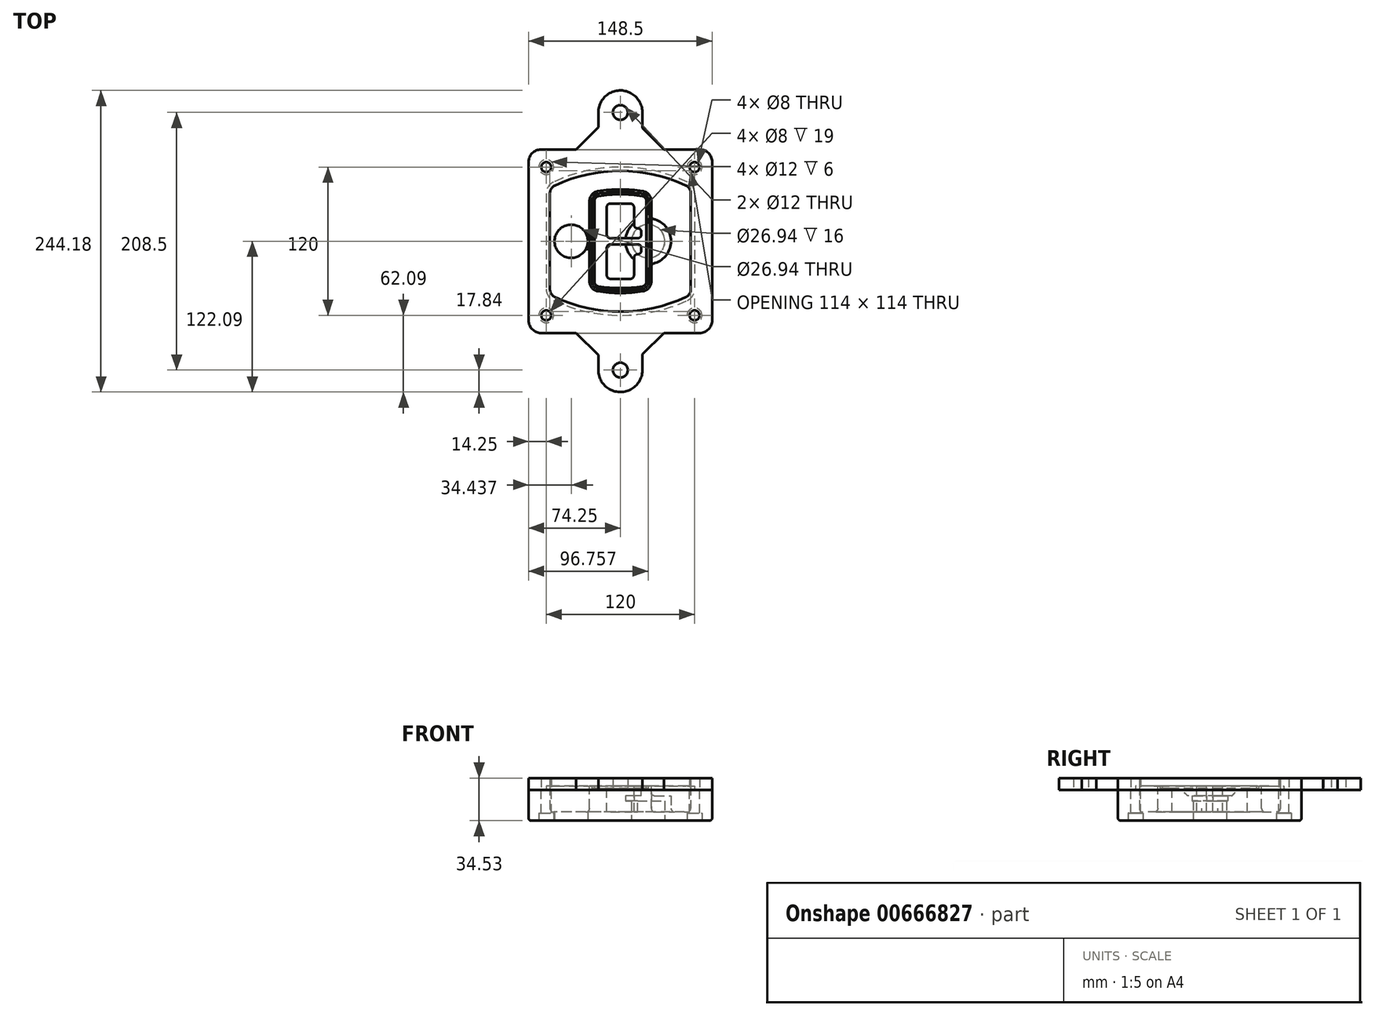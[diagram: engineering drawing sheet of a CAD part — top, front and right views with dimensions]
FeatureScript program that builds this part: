
annotation { "Feature Type Name" : "Feature", "Feature Type Description" : "" }
export const myFeature = defineFeature(function(context is Context, id is Id, definition is map)
    precondition{}
    {
        {
            var Q0;
            Q0=qCreatedBy(makeId("Top.planeOp"),FACE);
            var sketch = newSketch(context, id + "F0", { "sketchPlane" : qUnion([Q0])});
            skPoint(sketch, "E0.rect.middle", {"position": v(0, 0) * mm});
            skLineSegment(sketch, "E1.bottom", {"start": v(-64.25, -74.25) * mm, "end": v(64.25, -74.25) * mm});
            skLineSegment(sketch, "E1.top", {"start": v(-64.25, 74.25) * mm, "end": v(64.25, 74.25) * mm});
            skLineSegment(sketch, "E1.left", {"start": v(-74.25, -64.25) * mm, "end": v(-74.25, 64.25) * mm});
            skLineSegment(sketch, "E1.right", {"start": v(74.25, -64.25) * mm, "end": v(74.25, 64.25) * mm});
            skLineSegment(sketch, "E2", {"start": v(-74.25, 74.25) * mm, "end": v(74.25, -74.25) * mm, "construction": true});
            skLineSegment(sketch, "E3", {"start": v(74.25, 74.25) * mm, "end": v(-74.25, -74.25) * mm, "construction": true});
            skCircle(sketch, "E4", {"center": v(-60, 60) * mm, "radius": 4 * mm});
            skCircle(sketch, "E5", {"center": v(60, 60) * mm, "radius": 4 * mm});
            skCircle(sketch, "E6", {"center": v(60, -60) * mm, "radius": 4 * mm});
            skCircle(sketch, "E7", {"center": v(-60, -60) * mm, "radius": 4 * mm});
            skLineSegment(sketch, "E8", {"start": v(-60, 60) * mm, "end": v(60, 60) * mm, "construction": true});
            skLineSegment(sketch, "E9", {"start": v(60, 60) * mm, "end": v(60, -60) * mm, "construction": true});
            skLineSegment(sketch, "E10", {"start": v(60, -60) * mm, "end": v(-60, -60) * mm, "construction": true});
            skLineSegment(sketch, "E11", {"start": v(-60, -60) * mm, "end": v(-60, 60) * mm, "construction": true});
            skLineSegment(sketch, "E12", {"start": v(-60, 38.83) * mm, "end": v(-60, -38.83) * mm});
            skLineSegment(sketch, "E13", {"start": v(60, 38.83) * mm, "end": v(60, -38.83) * mm});
            skArc(sketch, "E14", {"start": v(54.26, 47.88) * mm, "mid": v(0, 60) * mm, "end": v(-54.26, 47.88) * mm});
            skArc(sketch, "E15", {"start": v(-54.26, -47.88) * mm, "mid": v(0, -60) * mm, "end": v(54.26, -47.88) * mm});
            skLineSegment(sketch, "E16", {"start": v(-60, 0) * mm, "end": v(60, 0) * mm, "construction": true});
            skPoint(sketch, "E17.visualSharp", {"position": v(-60, -45) * mm});
            skArc(sketch, "E17.filletArc", {"start": v(-60, -38.83) * mm, "mid": v(-58.44, -44.2) * mm, "end": v(-54.26, -47.88) * mm});
            skPoint(sketch, "E18.visualSharp", {"position": v(-60, 45) * mm});
            skArc(sketch, "E18.filletArc", {"start": v(-54.26, 47.88) * mm, "mid": v(-58.44, 44.2) * mm, "end": v(-60, 38.83) * mm});
            skPoint(sketch, "E19.visualSharp", {"position": v(60, 45) * mm});
            skArc(sketch, "E19.filletArc", {"start": v(60, 38.83) * mm, "mid": v(58.44, 44.2) * mm, "end": v(54.26, 47.88) * mm});
            skPoint(sketch, "E20.visualSharp", {"position": v(60, -45) * mm});
            skArc(sketch, "E20.filletArc", {"start": v(54.26, -47.88) * mm, "mid": v(58.44, -44.2) * mm, "end": v(60, -38.83) * mm});
            skPoint(sketch, "E21.visualSharp", {"position": v(-74.25, 74.25) * mm});
            skArc(sketch, "E21.filletArc", {"start": v(-64.25, 74.25) * mm, "mid": v(-71.32, 71.32) * mm, "end": v(-74.25, 64.25) * mm});
            skPoint(sketch, "E22.visualSharp", {"position": v(74.25, 74.25) * mm});
            skArc(sketch, "E22.filletArc", {"start": v(74.25, 64.25) * mm, "mid": v(71.32, 71.32) * mm, "end": v(64.25, 74.25) * mm});
            skPoint(sketch, "E23.visualSharp", {"position": v(74.25, -74.25) * mm});
            skArc(sketch, "E23.filletArc", {"start": v(64.25, -74.25) * mm, "mid": v(71.32, -71.32) * mm, "end": v(74.25, -64.25) * mm});
            skPoint(sketch, "E24.visualSharp", {"position": v(-74.25, -74.25) * mm});
            skArc(sketch, "E24.filletArc", {"start": v(-74.25, -64.25) * mm, "mid": v(-71.32, -71.32) * mm, "end": v(-64.25, -74.25) * mm});
            skArc(sketch, "E25.0", {"start": v(57, 38.83) * mm, "mid": v(55.9, 42.58) * mm, "end": v(52.98, 45.17) * mm});
            skLineSegment(sketch, "E25.1", {"start": v(57, 38.83) * mm, "end": v(57, -38.83) * mm});
            skArc(sketch, "E25.2", {"start": v(52.98, -45.17) * mm, "mid": v(55.9, -42.58) * mm, "end": v(57, -38.83) * mm});
            skArc(sketch, "E25.3", {"start": v(-52.98, -45.17) * mm, "mid": v(0, -57) * mm, "end": v(52.98, -45.17) * mm});
            skArc(sketch, "E25.4", {"start": v(-57, -38.83) * mm, "mid": v(-55.9, -42.58) * mm, "end": v(-52.98, -45.17) * mm});
            skArc(sketch, "E25.5", {"start": v(52.98, 45.17) * mm, "mid": v(0, 57) * mm, "end": v(-52.98, 45.17) * mm});
            skLineSegment(sketch, "E25.6", {"start": v(-57, 38.83) * mm, "end": v(-57, -38.83) * mm});
            skArc(sketch, "E25.7", {"start": v(-52.98, 45.17) * mm, "mid": v(-55.9, 42.58) * mm, "end": v(-57, 38.83) * mm});
            skArc(sketch, "E26.0", {"start": v(-55.96, 51.5) * mm, "mid": v(-61.82, 46.33) * mm, "end": v(-64, 38.83) * mm});
            skArc(sketch, "E26.1", {"start": v(55.96, 51.5) * mm, "mid": v(0, 64) * mm, "end": v(-55.96, 51.5) * mm});
            skArc(sketch, "E26.2", {"start": v(64, 38.83) * mm, "mid": v(61.82, 46.33) * mm, "end": v(55.96, 51.5) * mm});
            skLineSegment(sketch, "E26.3", {"start": v(64, 38.83) * mm, "end": v(64, -38.83) * mm});
            skArc(sketch, "E26.4", {"start": v(55.96, -51.5) * mm, "mid": v(61.82, -46.33) * mm, "end": v(64, -38.83) * mm});
            skLineSegment(sketch, "E26.5", {"start": v(-64, 38.83) * mm, "end": v(-64, -38.83) * mm});
            skArc(sketch, "E26.6", {"start": v(-55.96, -51.5) * mm, "mid": v(0, -64) * mm, "end": v(55.96, -51.5) * mm});
            skArc(sketch, "E26.7", {"start": v(-64, -38.83) * mm, "mid": v(-61.82, -46.33) * mm, "end": v(-55.96, -51.5) * mm});
            skSolve(sketch);
        }
        {
            var Q0;
            Q0=makeQuery(id+"F0.imprint","IMPRINT",FACE,{"disambiguationData":[TD([[makeQuery(id+"F0.imprint","IMPRINT",EDGE,{"derivedFrom":sQuery(id+"F0.wireOp",EDGE,"E1.bottom")}),1.0]])]});
            var Q1;
            Q1=makeQuery(id+"F0.imprint","IMPRINT",FACE,{"disambiguationData":[TD([[makeQuery(id+"F0.imprint","IMPRINT",EDGE,{"derivedFrom":sQuery(id+"F0.wireOp",EDGE,"E12")}),1.0]])]});
            var Q2;
            Q2=makeQuery(id+"F0.imprint","IMPRINT",FACE,{"disambiguationData":[TD([[makeQuery(id+"F0.imprint","IMPRINT",EDGE,{"derivedFrom":sQuery(id+"F0.wireOp",EDGE,"E25.0")}),1.0]])]});
            var Q3;
            Q3=makeQuery(id+"F0.imprint","IMPRINT",FACE,{"disambiguationData":[TD([[makeQuery(id+"F0.imprint","IMPRINT",EDGE,{"derivedFrom":sQuery(id+"F0.wireOp",EDGE,"E12")}),-1.0]])]});
            extrude(context, id + "F1", {"entities" : qUnion([Q0, Q1, Q2, Q3]), "oppositeDirection" : true, "depth" : 25 * mm});
        }
        {
            var Q0;
            Q0=makeQuery(id+"F0.imprint","IMPRINT",FACE,{"disambiguationData":[TD([[makeQuery(id+"F0.imprint","IMPRINT",EDGE,{"derivedFrom":sQuery(id+"F0.wireOp",EDGE,"E12")}),1.0]])]});
            extrude(context, id + "F2", {"entities" : qUnion([Q0]), "operationType" : NewBodyOperationType.ADD, "depth" : 3 * mm});
        }
        {
            var Q0;
            Q0=makeQuery(id+"F0.imprint","IMPRINT",FACE,{"disambiguationData":[TD([[makeQuery(id+"F0.imprint","IMPRINT",EDGE,{"derivedFrom":sQuery(id+"F0.wireOp",EDGE,"E25.0")}),1.0]])]});
            extrude(context, id + "F3", {"entities" : qUnion([Q0]), "operationType" : NewBodyOperationType.REMOVE, "oppositeDirection" : true, "depth" : 18 * mm});
        }
        {
            var Q0;
            Q0=makeQuery(id+"F2.opExtrude","CAP_FACE",FACE,{"disambiguationData":[OSD([sQuery(id+"F0.wireOp",EDGE,"E12"),sQuery(id+"F0.wireOp",EDGE,"E13"),sQuery(id+"F0.wireOp",EDGE,"E14"),sQuery(id+"F0.wireOp",EDGE,"E15"),sQuery(id+"F0.wireOp",EDGE,"E17.filletArc"),sQuery(id+"F0.wireOp",EDGE,"E18.filletArc"),sQuery(id+"F0.wireOp",EDGE,"E19.filletArc"),sQuery(id+"F0.wireOp",EDGE,"E20.filletArc"),sQuery(id+"F0.wireOp",EDGE,"E25.0"),sQuery(id+"F0.wireOp",EDGE,"E25.1"),sQuery(id+"F0.wireOp",EDGE,"E25.2"),sQuery(id+"F0.wireOp",EDGE,"E25.3"),sQuery(id+"F0.wireOp",EDGE,"E25.4"),sQuery(id+"F0.wireOp",EDGE,"E25.5"),sQuery(id+"F0.wireOp",EDGE,"E25.6"),sQuery(id+"F0.wireOp",EDGE,"E25.7")])],"isStart":false});
            var sketch = newSketch(context, id + "F4", { "sketchPlane" : qUnion([Q0])});
            skArc(sketch, "E27.0", {"start": v(-18.34, -40.45) * mm, "mid": v(0, -42) * mm, "end": v(18.34, -40.45) * mm});
            skArc(sketch, "E28.0", {"start": v(18.34, 40.45) * mm, "mid": v(0, 42) * mm, "end": v(-18.34, 40.45) * mm});
            skLineSegment(sketch, "E29", {"start": v(-25, 32.57) * mm, "end": v(-25, -32.57) * mm});
            skLineSegment(sketch, "E30", {"start": v(25, 32.57) * mm, "end": v(25, -32.57) * mm});
            skLineSegment(sketch, "E31", {"start": v(-25, 39.1) * mm, "end": v(25, 39.1) * mm, "construction": true});
            skLineSegment(sketch, "E32", {"start": v(-25, -39.1) * mm, "end": v(25, -39.1) * mm, "construction": true});
            skPoint(sketch, "E33.visualSharp", {"position": v(-25, 39.1) * mm});
            skArc(sketch, "E33.filletArc", {"start": v(-18.34, 40.45) * mm, "mid": v(-23.11, 37.73) * mm, "end": v(-25, 32.57) * mm});
            skPoint(sketch, "E34.visualSharp", {"position": v(25, 39.1) * mm});
            skArc(sketch, "E34.filletArc", {"start": v(25, 32.57) * mm, "mid": v(23.11, 37.73) * mm, "end": v(18.34, 40.45) * mm});
            skPoint(sketch, "E35.visualSharp", {"position": v(25, -39.1) * mm});
            skArc(sketch, "E35.filletArc", {"start": v(18.34, -40.45) * mm, "mid": v(23.11, -37.73) * mm, "end": v(25, -32.57) * mm});
            skPoint(sketch, "E36.visualSharp", {"position": v(-25, -39.1) * mm});
            skArc(sketch, "E36.filletArc", {"start": v(-25, -32.57) * mm, "mid": v(-23.11, -37.73) * mm, "end": v(-18.34, -40.45) * mm});
            skArc(sketch, "E37.0", {"start": v(52.98, 45.17) * mm, "mid": v(0, 57) * mm, "end": v(-52.98, 45.17) * mm});
            skArc(sketch, "E37.1", {"start": v(-52.98, 45.17) * mm, "mid": v(-55.9, 42.58) * mm, "end": v(-57, 38.83) * mm});
            skLineSegment(sketch, "E37.2", {"start": v(-57, 38.83) * mm, "end": v(-57, -38.83) * mm});
            skArc(sketch, "E37.3", {"start": v(-57, -38.83) * mm, "mid": v(-55.9, -42.58) * mm, "end": v(-52.98, -45.17) * mm});
            skArc(sketch, "E37.4", {"start": v(-52.98, -45.17) * mm, "mid": v(0, -57) * mm, "end": v(52.98, -45.17) * mm});
            skArc(sketch, "E37.5", {"start": v(52.98, -45.17) * mm, "mid": v(55.9, -42.58) * mm, "end": v(57, -38.83) * mm});
            skLineSegment(sketch, "E37.6", {"start": v(57, 38.83) * mm, "end": v(57, -38.83) * mm});
            skArc(sketch, "E37.7", {"start": v(57, 38.83) * mm, "mid": v(55.9, 42.58) * mm, "end": v(52.98, 45.17) * mm});
            skLineSegment(sketch, "E38.0", {"start": v(23, 32.57) * mm, "end": v(23, -32.57) * mm});
            skArc(sketch, "E38.1", {"start": v(18, -38.48) * mm, "mid": v(21.58, -36.44) * mm, "end": v(23, -32.57) * mm});
            skArc(sketch, "E38.2", {"start": v(-18, -38.48) * mm, "mid": v(0, -40) * mm, "end": v(18, -38.48) * mm});
            skArc(sketch, "E38.3", {"start": v(-23, -32.57) * mm, "mid": v(-21.58, -36.44) * mm, "end": v(-18, -38.48) * mm});
            skLineSegment(sketch, "E38.4", {"start": v(-23, 32.57) * mm, "end": v(-23, -32.57) * mm});
            skArc(sketch, "E38.5", {"start": v(23, 32.57) * mm, "mid": v(21.58, 36.44) * mm, "end": v(18, 38.48) * mm});
            skArc(sketch, "E38.6", {"start": v(-18, 38.48) * mm, "mid": v(-21.58, 36.44) * mm, "end": v(-23, 32.57) * mm});
            skArc(sketch, "E38.7", {"start": v(18, 38.48) * mm, "mid": v(0, 40) * mm, "end": v(-18, 38.48) * mm});
            skArc(sketch, "E39.0", {"start": v(21, 32.57) * mm, "mid": v(20.06, 35.15) * mm, "end": v(17.67, 36.5) * mm});
            skLineSegment(sketch, "E39.1", {"start": v(21, 32.57) * mm, "end": v(21, -32.57) * mm});
            skArc(sketch, "E39.2", {"start": v(17.67, -36.5) * mm, "mid": v(20.06, -35.15) * mm, "end": v(21, -32.57) * mm});
            skArc(sketch, "E39.3", {"start": v(-17.67, -36.5) * mm, "mid": v(0, -38) * mm, "end": v(17.67, -36.5) * mm});
            skArc(sketch, "E39.4", {"start": v(-21, -32.57) * mm, "mid": v(-20.06, -35.15) * mm, "end": v(-17.67, -36.5) * mm});
            skArc(sketch, "E39.5", {"start": v(17.67, 36.5) * mm, "mid": v(0, 38) * mm, "end": v(-17.67, 36.5) * mm});
            skLineSegment(sketch, "E39.6", {"start": v(-21, 32.57) * mm, "end": v(-21, -32.57) * mm});
            skArc(sketch, "E39.7", {"start": v(-17.67, 36.5) * mm, "mid": v(-20.06, 35.15) * mm, "end": v(-21, 32.57) * mm});
            skLineSegment(sketch, "E40", {"start": v(-25, 0) * mm, "end": v(25, 0) * mm, "construction": true});
            skLineSegment(sketch, "E41", {"start": v(-11, 5.5) * mm, "end": v(-11, 27.5) * mm});
            skLineSegment(sketch, "E42", {"start": v(-8, 30.5) * mm, "end": v(8, 30.5) * mm});
            skLineSegment(sketch, "E43", {"start": v(11, 27.5) * mm, "end": v(11, 13.5) * mm});
            skLineSegment(sketch, "E44", {"start": v(14, 10.5) * mm, "end": v(14, 10.5) * mm});
            skLineSegment(sketch, "E45", {"start": v(17, 7.5) * mm, "end": v(17, 5.5) * mm});
            skLineSegment(sketch, "E46", {"start": v(14, 2.5) * mm, "end": v(-8, 2.5) * mm});
            skPoint(sketch, "E47.visualSharp", {"position": v(-11, 30.5) * mm});
            skArc(sketch, "E47.filletArc", {"start": v(-8, 30.5) * mm, "mid": v(-10.12, 29.62) * mm, "end": v(-11, 27.5) * mm});
            skPoint(sketch, "E48.visualSharp", {"position": v(11, 30.5) * mm});
            skArc(sketch, "E48.filletArc", {"start": v(11, 27.5) * mm, "mid": v(10.12, 29.62) * mm, "end": v(8, 30.5) * mm});
            skPoint(sketch, "E49.visualSharp", {"position": v(11, 10.5) * mm});
            skArc(sketch, "E49.filletArc", {"start": v(11, 13.5) * mm, "mid": v(11.88, 11.38) * mm, "end": v(14, 10.5) * mm});
            skPoint(sketch, "E50.visualSharp", {"position": v(17, 10.5) * mm});
            skArc(sketch, "E50.filletArc", {"start": v(17, 7.5) * mm, "mid": v(16.12, 9.62) * mm, "end": v(14, 10.5) * mm});
            skPoint(sketch, "E51.visualSharp", {"position": v(17, 2.5) * mm});
            skArc(sketch, "E51.filletArc", {"start": v(14, 2.5) * mm, "mid": v(16.12, 3.38) * mm, "end": v(17, 5.5) * mm});
            skPoint(sketch, "E52.visualSharp", {"position": v(-11, 2.5) * mm});
            skArc(sketch, "E52.filletArc", {"start": v(-11, 5.5) * mm, "mid": v(-10.12, 3.38) * mm, "end": v(-8, 2.5) * mm});
            skLineSegment(sketch, "E53.0.MirrorCS", {"start": v(14, -2.5) * mm, "end": v(-8, -2.5) * mm});
            skArc(sketch, "E54.0.MirrorCS", {"start": v(-11, -5.5) * mm, "mid": v(-10.12, -3.38) * mm, "end": v(-8, -2.5) * mm});
            skLineSegment(sketch, "E55.0.MirrorCS", {"start": v(-11, -5.5) * mm, "end": v(-11, -27.5) * mm});
            skArc(sketch, "E56.0.MirrorCS", {"start": v(-8, -30.5) * mm, "mid": v(-10.12, -29.62) * mm, "end": v(-11, -27.5) * mm});
            skLineSegment(sketch, "E57.0.MirrorCS", {"start": v(-8, -30.5) * mm, "end": v(8, -30.5) * mm});
            skArc(sketch, "E58.0.MirrorCS", {"start": v(11, -27.5) * mm, "mid": v(10.12, -29.62) * mm, "end": v(8, -30.5) * mm});
            skLineSegment(sketch, "E59.0.MirrorCS", {"start": v(11, -27.5) * mm, "end": v(11, -13.5) * mm});
            skArc(sketch, "E60.0.MirrorCS", {"start": v(11, -13.5) * mm, "mid": v(11.88, -11.38) * mm, "end": v(14, -10.5) * mm});
            skArc(sketch, "E61.0.MirrorCS", {"start": v(17, -7.5) * mm, "mid": v(16.12, -9.62) * mm, "end": v(14, -10.5) * mm});
            skLineSegment(sketch, "E62.0.MirrorCS", {"start": v(17, -7.5) * mm, "end": v(17, -5.5) * mm});
            skArc(sketch, "E63.0.MirrorCS", {"start": v(14, -2.5) * mm, "mid": v(16.12, -3.38) * mm, "end": v(17, -5.5) * mm});
            skSolve(sketch);
        }
        {
            var Q0;
            Q0=makeQuery(id+"F4.imprint","IMPRINT",FACE,{"disambiguationData":[TD([[makeQuery(id+"F4.imprint","IMPRINT",EDGE,{"derivedFrom":sQuery(id+"F4.wireOp",EDGE,"E27.0")}),1.0]])]});
            var Q1;
            Q1=makeQuery(id+"F4.imprint","IMPRINT",FACE,{"disambiguationData":[TD([[makeQuery(id+"F4.imprint","IMPRINT",EDGE,{"derivedFrom":sQuery(id+"F4.wireOp",EDGE,"E38.0")}),-1.0]])]});
            var Q2;
            Q2=makeQuery(id+"F4.imprint","IMPRINT",FACE,{"disambiguationData":[TD([[makeQuery(id+"F4.imprint","IMPRINT",EDGE,{"derivedFrom":sQuery(id+"F4.wireOp",EDGE,"E39.0")}),1.0]])]});
            extrude(context, id + "F5", {"entities" : qUnion([Q0, Q1, Q2]), "operationType" : NewBodyOperationType.ADD, "endBound" : BoundingType.UP_TO_NEXT, "oppositeDirection" : true, "depth" : 25 * mm});
        }
        {
            var Q0;
            Q0=makeQuery(id+"F4.imprint","IMPRINT",FACE,{"disambiguationData":[TD([[makeQuery(id+"F4.imprint","IMPRINT",EDGE,{"derivedFrom":sQuery(id+"F4.wireOp",EDGE,"E38.0")}),-1.0]])]});
            extrude(context, id + "F6", {"entities" : qUnion([Q0]), "operationType" : NewBodyOperationType.REMOVE, "oppositeDirection" : true, "depth" : 2 * mm});
        }
        {
            var Q0;
            Q0=makeQuery(id+"F1.opExtrude","CAP_FACE",FACE,{"disambiguationData":[OSD([sQuery(id+"F0.wireOp",EDGE,"E1.bottom"),sQuery(id+"F0.wireOp",EDGE,"E1.top"),sQuery(id+"F0.wireOp",EDGE,"E1.left"),sQuery(id+"F0.wireOp",EDGE,"E1.right"),sQuery(id+"F0.wireOp",EDGE,"E4"),sQuery(id+"F0.wireOp",EDGE,"E5"),sQuery(id+"F0.wireOp",EDGE,"E6"),sQuery(id+"F0.wireOp",EDGE,"E7"),sQuery(id+"F0.wireOp",EDGE,"E21.filletArc"),sQuery(id+"F0.wireOp",EDGE,"E22.filletArc"),sQuery(id+"F0.wireOp",EDGE,"E23.filletArc"),sQuery(id+"F0.wireOp",EDGE,"E24.filletArc")])],"isStart":false});
            var sketch = newSketch(context, id + "F7", { "sketchPlane" : qUnion([Q0])});
            skCircle(sketch, "E64", {"center": v(22.5, 0) * mm, "radius": 13.47 * mm});
            skCircle(sketch, "E65", {"center": v(-39.81, 0) * mm, "radius": 13.47 * mm});
            skLineSegment(sketch, "E66", {"start": v(74.25, 0) * mm, "end": v(-74.25, 0) * mm});
            skCircle(sketch, "E67", {"center": v(22.5, 0) * mm, "radius": 18.47 * mm});
            skCircle(sketch, "E68", {"center": v(60, -60) * mm, "radius": 6 * mm});
            skCircle(sketch, "E69", {"center": v(-60, -60) * mm, "radius": 6 * mm});
            skCircle(sketch, "E70", {"center": v(-60, 60) * mm, "radius": 6 * mm});
            skCircle(sketch, "E71", {"center": v(60, 60) * mm, "radius": 6 * mm});
            skSolve(sketch);
        }
        {
            var Q0;
            {var subQ1=sQuery(id+"F7.wireOp",EDGE,"E66");var subQ4=sQuery(id+"F7.wireOp",EDGE,"E64");var subQ6=makeQuery(id+"F7.imprint","INTERSECT",VERTEX,{"disambiguationData":[OD(0.0)],"derivedFrom":[subQ4,subQ1]});Q0=makeQuery(id+"F7.imprint","IMPRINT",FACE,{"disambiguationData":[TD([[makeQuery(id+"F7.imprint","IMPRINT",EDGE,{"disambiguationData":[TD([[subQ6,-1.0]])],"derivedFrom":subQ4}),-1.0]])]});}
            var Q1;
            {var subQ0=sQuery(id+"F7.wireOp",EDGE,"E66");var subQ1=sQuery(id+"F7.wireOp",EDGE,"E64");var subQ3=makeQuery(id+"F7.imprint","INTERSECT",VERTEX,{"disambiguationData":[OD(0.0)],"derivedFrom":[subQ1,subQ0]});Q1=makeQuery(id+"F7.imprint","IMPRINT",FACE,{"disambiguationData":[TD([[makeQuery(id+"F7.imprint","IMPRINT",EDGE,{"disambiguationData":[TD([[subQ3,-1.0]])],"derivedFrom":subQ1}),1.0]])]});}
            var Q2;
            {var subQ0=sQuery(id+"F7.wireOp",EDGE,"E66");var subQ1=sQuery(id+"F7.wireOp",EDGE,"E64");var subQ3=makeQuery(id+"F7.imprint","INTERSECT",VERTEX,{"disambiguationData":[OD(0.0)],"derivedFrom":[subQ1,subQ0]});Q2=makeQuery(id+"F7.imprint","IMPRINT",FACE,{"disambiguationData":[TD([[makeQuery(id+"F7.imprint","IMPRINT",EDGE,{"disambiguationData":[TD([[subQ3,1.0]])],"derivedFrom":subQ1}),1.0]])]});}
            var Q3;
            {var subQ1=sQuery(id+"F7.wireOp",EDGE,"E66");var subQ4=sQuery(id+"F7.wireOp",EDGE,"E64");var subQ6=makeQuery(id+"F7.imprint","INTERSECT",VERTEX,{"disambiguationData":[OD(0.0)],"derivedFrom":[subQ4,subQ1]});Q3=makeQuery(id+"F7.imprint","IMPRINT",FACE,{"disambiguationData":[TD([[makeQuery(id+"F7.imprint","IMPRINT",EDGE,{"disambiguationData":[TD([[subQ6,1.0]])],"derivedFrom":subQ4}),-1.0]])]});}
            extrude(context, id + "F8", {"entities" : qUnion([Q0, Q1, Q2, Q3]), "operationType" : NewBodyOperationType.ADD, "oppositeDirection" : true, "depth" : 20 * mm});
        }
        {
            var Q0;
            {var subQ0=sQuery(id+"F7.wireOp",EDGE,"E66");var subQ1=sQuery(id+"F7.wireOp",EDGE,"E64");var subQ3=makeQuery(id+"F7.imprint","INTERSECT",VERTEX,{"disambiguationData":[OD(0.0)],"derivedFrom":[subQ1,subQ0]});Q0=makeQuery(id+"F7.imprint","IMPRINT",FACE,{"disambiguationData":[TD([[makeQuery(id+"F7.imprint","IMPRINT",EDGE,{"disambiguationData":[TD([[subQ3,-1.0]])],"derivedFrom":subQ1}),1.0]])]});}
            var Q1;
            {var subQ0=sQuery(id+"F7.wireOp",EDGE,"E66");var subQ1=sQuery(id+"F7.wireOp",EDGE,"E64");var subQ3=makeQuery(id+"F7.imprint","INTERSECT",VERTEX,{"disambiguationData":[OD(0.0)],"derivedFrom":[subQ1,subQ0]});Q1=makeQuery(id+"F7.imprint","IMPRINT",FACE,{"disambiguationData":[TD([[makeQuery(id+"F7.imprint","IMPRINT",EDGE,{"disambiguationData":[TD([[subQ3,1.0]])],"derivedFrom":subQ1}),1.0]])]});}
            extrude(context, id + "F9", {"entities" : qUnion([Q0, Q1]), "operationType" : NewBodyOperationType.REMOVE, "oppositeDirection" : true, "depth" : 16 * mm});
        }
        {
            var Q0;
            {var subQ0=sQuery(id+"F7.wireOp",EDGE,"E66");var subQ1=sQuery(id+"F7.wireOp",EDGE,"E65");var subQ3=makeQuery(id+"F7.imprint","INTERSECT",VERTEX,{"disambiguationData":[OD(0.0)],"derivedFrom":[subQ1,subQ0]});Q0=makeQuery(id+"F7.imprint","IMPRINT",FACE,{"disambiguationData":[TD([[makeQuery(id+"F7.imprint","IMPRINT",EDGE,{"disambiguationData":[TD([[subQ3,-1.0]])],"derivedFrom":subQ1}),1.0]])]});}
            var Q1;
            {var subQ0=sQuery(id+"F7.wireOp",EDGE,"E66");var subQ1=sQuery(id+"F7.wireOp",EDGE,"E65");var subQ3=makeQuery(id+"F7.imprint","INTERSECT",VERTEX,{"disambiguationData":[OD(0.0)],"derivedFrom":[subQ1,subQ0]});Q1=makeQuery(id+"F7.imprint","IMPRINT",FACE,{"disambiguationData":[TD([[makeQuery(id+"F7.imprint","IMPRINT",EDGE,{"disambiguationData":[TD([[subQ3,1.0]])],"derivedFrom":subQ1}),1.0]])]});}
            extrude(context, id + "F10", {"entities" : qUnion([Q0, Q1]), "operationType" : NewBodyOperationType.REMOVE, "oppositeDirection" : true, "depth" : 25 * mm});
        }
        {
            var Q0;
            Q0=makeQuery(id+"F7.imprint","IMPRINT",FACE,{"disambiguationData":[TD([[makeQuery(id+"F7.imprint","IMPRINT",EDGE,{"derivedFrom":sQuery(id+"F7.wireOp",EDGE,"E68")}),1.0]])]});
            var Q1;
            Q1=makeQuery(id+"F7.imprint","IMPRINT",FACE,{"disambiguationData":[TD([[makeQuery(id+"F7.imprint","IMPRINT",EDGE,{"derivedFrom":makeQuery(id+"F1.opExtrude","CAP_EDGE",EDGE,{"disambiguationData":[OSD([sQuery(id+"F0.wireOp",EDGE,"E5")])],"isStart":false})}),-1.0]])]});
            var Q2;
            Q2=makeQuery(id+"F7.imprint","IMPRINT",FACE,{"disambiguationData":[TD([[makeQuery(id+"F7.imprint","IMPRINT",EDGE,{"derivedFrom":sQuery(id+"F7.wireOp",EDGE,"E69")}),1.0]])]});
            var Q3;
            Q3=makeQuery(id+"F7.imprint","IMPRINT",FACE,{"disambiguationData":[TD([[makeQuery(id+"F7.imprint","IMPRINT",EDGE,{"derivedFrom":makeQuery(id+"F1.opExtrude","CAP_EDGE",EDGE,{"disambiguationData":[OSD([sQuery(id+"F0.wireOp",EDGE,"E4")])],"isStart":false})}),-1.0]])]});
            var Q4;
            Q4=makeQuery(id+"F7.imprint","IMPRINT",FACE,{"disambiguationData":[TD([[makeQuery(id+"F7.imprint","IMPRINT",EDGE,{"derivedFrom":sQuery(id+"F7.wireOp",EDGE,"E70")}),1.0]])]});
            var Q5;
            Q5=makeQuery(id+"F7.imprint","IMPRINT",FACE,{"disambiguationData":[TD([[makeQuery(id+"F7.imprint","IMPRINT",EDGE,{"derivedFrom":makeQuery(id+"F1.opExtrude","CAP_EDGE",EDGE,{"disambiguationData":[OSD([sQuery(id+"F0.wireOp",EDGE,"E7")])],"isStart":false})}),-1.0]])]});
            var Q6;
            Q6=makeQuery(id+"F7.imprint","IMPRINT",FACE,{"disambiguationData":[TD([[makeQuery(id+"F7.imprint","IMPRINT",EDGE,{"derivedFrom":sQuery(id+"F7.wireOp",EDGE,"E71")}),1.0]])]});
            var Q7;
            Q7=makeQuery(id+"F7.imprint","IMPRINT",FACE,{"disambiguationData":[TD([[makeQuery(id+"F7.imprint","IMPRINT",EDGE,{"derivedFrom":makeQuery(id+"F1.opExtrude","CAP_EDGE",EDGE,{"disambiguationData":[OSD([sQuery(id+"F0.wireOp",EDGE,"E6")])],"isStart":false})}),-1.0]])]});
            extrude(context, id + "F11", {"entities" : qUnion([Q0, Q1, Q2, Q3, Q4, Q5, Q6, Q7]), "operationType" : NewBodyOperationType.REMOVE, "oppositeDirection" : true, "depth" : 6 * mm});
        }
        {
            var Q0;
            Q0=makeQuery(id+"F9.boolean.opBoolean","COPY",FACE,{"derivedFrom":makeQuery(id+"F9.opExtrude","CAP_FACE",FACE,{"disambiguationData":[OSD([sQuery(id+"F7.wireOp",EDGE,"E64")])],"isStart":false})});
            var sketch = newSketch(context, id + "F12", { "sketchPlane" : qUnion([Q0])});
            skArc(sketch, "E72.0", {"start": v(11, 14.45) * mm, "mid": v(6.45, 9.13) * mm, "end": v(4.2, 2.5) * mm});
            skArc(sketch, "E72.1", {"start": v(4.2, -2.5) * mm, "mid": v(6.45, -9.13) * mm, "end": v(11, -14.45) * mm});
            skLineSegment(sketch, "E73", {"start": v(4.2, -2.5) * mm, "end": v(14, -2.5) * mm});
            skLineSegment(sketch, "E74.0", {"start": v(14, 2.5) * mm, "end": v(4.2, 2.5) * mm});
            skArc(sketch, "E74.1", {"start": v(14, 2.5) * mm, "mid": v(16.12, 3.38) * mm, "end": v(17, 5.5) * mm});
            skLineSegment(sketch, "E74.2", {"start": v(17, 7.5) * mm, "end": v(17, 5.5) * mm});
            skArc(sketch, "E74.3", {"start": v(17, 7.5) * mm, "mid": v(16.12, 9.62) * mm, "end": v(14, 10.5) * mm});
            skArc(sketch, "E74.4", {"start": v(11, 13.5) * mm, "mid": v(11.88, 11.38) * mm, "end": v(14, 10.5) * mm});
            skLineSegment(sketch, "E74.5", {"start": v(11, 14.45) * mm, "end": v(11, 13.5) * mm});
            skLineSegment(sketch, "E74.7", {"start": v(14, -2.5) * mm, "end": v(4.2, -2.5) * mm});
            skArc(sketch, "E74.8", {"start": v(14, -2.5) * mm, "mid": v(16.12, -3.38) * mm, "end": v(17, -5.5) * mm});
            skLineSegment(sketch, "E74.9", {"start": v(17, -7.5) * mm, "end": v(17, -5.5) * mm});
            skArc(sketch, "E74.10", {"start": v(17, -7.5) * mm, "mid": v(16.12, -9.62) * mm, "end": v(14, -10.5) * mm});
            skArc(sketch, "E74.11", {"start": v(11, -13.5) * mm, "mid": v(11.88, -11.38) * mm, "end": v(14, -10.5) * mm});
            skLineSegment(sketch, "E74.12", {"start": v(11, -14.45) * mm, "end": v(11, -13.5) * mm});
            skPoint(sketch, "E75.orphan", {"position": v(11, -27.5) * mm});
            skPoint(sketch, "E76.orphan", {"position": v(-8, -2.5) * mm});
            skPoint(sketch, "E77.orphan", {"position": v(-8, 2.5) * mm});
            skPoint(sketch, "E78.orphan", {"position": v(11, 27.5) * mm});
            skSolve(sketch);
        }
        {
            var Q0;
            {var subQ7=sQuery(id+"F12.wireOp",EDGE,"E72.0");var subQ14=sQuery(id+"F12.wireOp",EDGE,"E72.1");var subQ16=sQuery(id+"F12.wireOp",EDGE,"E74.1");var subQ18=sQuery(id+"F12.wireOp",EDGE,"E74.8");Q0=qUnion([makeQuery(id+"F12.imprint","IMPRINT",FACE,{"disambiguationData":[TD([[makeQuery(id+"F12.imprint","IMPRINT",EDGE,{"derivedFrom":subQ7}),1.0]])]}),makeQuery(id+"F12.imprint","IMPRINT",FACE,{"disambiguationData":[TD([[makeQuery(id+"F12.imprint","IMPRINT",EDGE,{"derivedFrom":subQ14}),1.0]])]}),makeQuery(id+"F12.imprint","IMPRINT",FACE,{"disambiguationData":[TD([[makeQuery(id+"F12.imprint","IMPRINT",EDGE,{"derivedFrom":subQ16}),1.0]])]}),makeQuery(id+"F12.imprint","IMPRINT",FACE,{"disambiguationData":[TD([[makeQuery(id+"F12.imprint","IMPRINT",EDGE,{"derivedFrom":subQ18}),-1.0]])]})]);}
            var Q1;
            Q1=makeQuery(id+"F5.boolean.opBoolean","SPLIT",FACE,{"disambiguationData":[TD([makeQuery(id+"F5.opExtrude","SWEPT_FACE",FACE,{"disambiguationData":[OSD([sQuery(id+"F4.wireOp",EDGE,"E41")])]})])],"derivedFrom":makeQuery(id+"F3.boolean.opBoolean","COPY",FACE,{"derivedFrom":makeQuery(id+"F3.opExtrude","CAP_FACE",FACE,{"disambiguationData":[OSD([sQuery(id+"F0.wireOp",EDGE,"E25.0"),sQuery(id+"F0.wireOp",EDGE,"E25.1"),sQuery(id+"F0.wireOp",EDGE,"E25.2"),sQuery(id+"F0.wireOp",EDGE,"E25.3"),sQuery(id+"F0.wireOp",EDGE,"E25.4"),sQuery(id+"F0.wireOp",EDGE,"E25.5"),sQuery(id+"F0.wireOp",EDGE,"E25.6"),sQuery(id+"F0.wireOp",EDGE,"E25.7")])],"isStart":false})})});
            extrude(context, id + "F13", {"entities" : qUnion([Q0]), "operationType" : NewBodyOperationType.REMOVE, "endBound" : BoundingType.UP_TO_SURFACE, "endBoundEntityFace" : qUnion([Q1]), "depth" : 25 * mm});
        }
        {
            var Q0;
            Q0=makeQuery(id+"F3.boolean.opBoolean","COPY",EDGE,{"derivedFrom":makeQuery(id+"F3.opExtrude","CAP_EDGE",EDGE,{"disambiguationData":[OSD([sQuery(id+"F0.wireOp",EDGE,"E25.6")])],"isStart":false})});
            var Q1;
            Q1=makeQuery(id+"F8.boolean.opBoolean","INTERSECT",EDGE,{"derivedFrom":[makeQuery(id+"F5.opExtrude","SWEPT_FACE",FACE,{"disambiguationData":[OSD([sQuery(id+"F4.wireOp",EDGE,"E30")])]}),makeQuery(id+"F8.opExtrude","CAP_FACE",FACE,{"disambiguationData":[OSD([sQuery(id+"F7.wireOp",EDGE,"E67")])],"isStart":false})]});
            var Q2;
            Q2=makeQuery(id+"F8.boolean.opBoolean","INTERSECT",EDGE,{"disambiguationData":[OD(1.0)],"derivedFrom":[makeQuery(id+"F5.opExtrude","SWEPT_FACE",FACE,{"disambiguationData":[OSD([sQuery(id+"F4.wireOp",EDGE,"E30")])]}),makeQuery(id+"F8.opExtrude","SWEPT_FACE",FACE,{"disambiguationData":[OSD([sQuery(id+"F7.wireOp",EDGE,"E67")])]})]});
            var Q3;
            {var subQ0=sQuery(id+"F4.wireOp",EDGE,"E30");Q3=makeQuery(id+"F8.boolean.opBoolean","SPLIT",EDGE,{"disambiguationData":[TD([makeQuery(id+"F5.opExtrude","SWEPT_FACE",FACE,{"disambiguationData":[OSD([sQuery(id+"F4.wireOp",EDGE,"E35.filletArc")])]})])],"derivedFrom":makeQuery(id+"F5.opExtrude","CAP_EDGE",EDGE,{"disambiguationData":[OSD([subQ0])],"isStart":false})});}
            var Q4;
            {var subQ0=sQuery(id+"F0.wireOp",EDGE,"E25.7");var subQ1=sQuery(id+"F0.wireOp",EDGE,"E25.1");var subQ2=sQuery(id+"F0.wireOp",EDGE,"E25.6");var subQ3=sQuery(id+"F0.wireOp",EDGE,"E25.5");var subQ4=sQuery(id+"F0.wireOp",EDGE,"E25.4");var subQ5=sQuery(id+"F0.wireOp",EDGE,"E25.0");var subQ6=sQuery(id+"F0.wireOp",EDGE,"E25.2");var subQ7=sQuery(id+"F0.wireOp",EDGE,"E25.3");Q4=makeQuery(id+"F8.boolean.opBoolean","INTERSECT",EDGE,{"derivedFrom":[makeQuery(id+"F5.boolean.opBoolean","SPLIT",FACE,{"disambiguationData":[TD([makeQuery(id+"F2.opExtrude","SWEPT_FACE",FACE,{"disambiguationData":[OSD([subQ5])]})])],"derivedFrom":makeQuery(id+"F3.boolean.opBoolean","COPY",FACE,{"derivedFrom":makeQuery(id+"F3.opExtrude","CAP_FACE",FACE,{"disambiguationData":[OSD([subQ5,subQ1,subQ6,subQ7,subQ4,subQ3,subQ2,subQ0])],"isStart":false})})}),makeQuery(id+"F8.opExtrude","SWEPT_FACE",FACE,{"disambiguationData":[OSD([sQuery(id+"F7.wireOp",EDGE,"E67")])]})]});}
            var Q5;
            Q5=makeQuery(id+"F8.boolean.opBoolean","INTERSECT",EDGE,{"disambiguationData":[OD(0.0)],"derivedFrom":[makeQuery(id+"F5.opExtrude","SWEPT_FACE",FACE,{"disambiguationData":[OSD([sQuery(id+"F4.wireOp",EDGE,"E30")])]}),makeQuery(id+"F8.opExtrude","SWEPT_FACE",FACE,{"disambiguationData":[OSD([sQuery(id+"F7.wireOp",EDGE,"E67")])]})]});
            fillet(context, id + "F14", {"entities" : qUnion([Q0, Q1, Q2, Q3, Q4, Q5]), "radius" : 3 * mm, "tangentPropagation" : true, "allowEdgeOverflow" : false});
        }
        {
            var Q0;
            Q0=makeQuery(id+"F1.opExtrude","CAP_EDGE",EDGE,{"disambiguationData":[OSD([sQuery(id+"F0.wireOp",EDGE,"E1.bottom")])],"isStart":false});
            fillet(context, id + "F15", {"entities" : qUnion([Q0]), "radius" : 2 * mm, "tangentPropagation" : true, "allowEdgeOverflow" : false});
        }
        {
            var Q0;
            {var subQ0=sQuery(id+"F0.wireOp",EDGE,"E21.filletArc");var subQ1=sQuery(id+"F0.wireOp",EDGE,"E7");var subQ2=sQuery(id+"F0.wireOp",EDGE,"E6");var subQ3=sQuery(id+"F0.wireOp",EDGE,"E5");var subQ4=sQuery(id+"F0.wireOp",EDGE,"E4");var subQ5=sQuery(id+"F0.wireOp",EDGE,"E22.filletArc");var subQ6=sQuery(id+"F0.wireOp",EDGE,"E1.bottom");var subQ7=sQuery(id+"F0.wireOp",EDGE,"E1.right");var subQ8=sQuery(id+"F0.wireOp",EDGE,"E1.top");var subQ9=sQuery(id+"F0.wireOp",EDGE,"E1.left");var subQ10=sQuery(id+"F0.wireOp",EDGE,"E23.filletArc");var subQ11=sQuery(id+"F0.wireOp",EDGE,"E24.filletArc");Q0=makeQuery(id+"F2.boolean.opBoolean","SPLIT",FACE,{"disambiguationData":[TD([makeQuery(id+"F1.opExtrude","SWEPT_FACE",FACE,{"disambiguationData":[OSD([subQ6])]})])],"derivedFrom":makeQuery(id+"F1.opExtrude","CAP_FACE",FACE,{"disambiguationData":[OSD([subQ6,subQ8,subQ9,subQ7,subQ4,subQ3,subQ2,subQ1,subQ0,subQ5,subQ10,subQ11])],"isStart":true})});}
            var sketch = newSketch(context, id + "F16", { "sketchPlane" : qUnion([Q0])});
            skPoint(sketch, "E79.orphan", {"position": v(0, 74.25) * mm});
            skPoint(sketch, "E80.orphan", {"position": v(0, -74.25) * mm});
            skCircle(sketch, "E81", {"center": v(0, 104.25) * mm, "radius": 6 * mm});
            skLineSegment(sketch, "E82", {"start": v(-35.86, 74.25) * mm, "end": v(-17.84, 92.27) * mm});
            skPoint(sketch, "E83", {"position": v(0, 92.25) * mm});
            skArc(sketch, "E84", {"start": v(-17.84, 104.25) * mm, "mid": v(0.32, 122.08) * mm, "end": v(17.83, 103.6) * mm});
            skLineSegment(sketch, "E85", {"start": v(-17.84, 104.25) * mm, "end": v(-17.84, 92.27) * mm});
            skLineSegment(sketch, "E86", {"start": v(17.83, 103.6) * mm, "end": v(17.83, 91.62) * mm});
            skLineSegment(sketch, "E87", {"start": v(17.83, 91.62) * mm, "end": v(35.2, 74.25) * mm});
            skPoint(sketch, "E88.start.orphan", {"position": v(74.25, 0) * mm});
            skPoint(sketch, "E89", {"position": v(-74.25, 0) * mm});
            skLineSegment(sketch, "E90", {"start": v(-74.25, 0) * mm, "end": v(74.25, 0) * mm, "construction": true});
            skLineSegment(sketch, "E91.MirrorCS", {"start": v(-17.84, -104.25) * mm, "end": v(-17.84, -92.27) * mm});
            skLineSegment(sketch, "E92.MirrorCS", {"start": v(-35.86, -74.25) * mm, "end": v(-17.84, -92.27) * mm});
            skCircle(sketch, "E93.MirrorC", {"center": v(0, -104.25) * mm, "radius": 6 * mm});
            skArc(sketch, "E94.MirrorCS", {"start": v(-17.84, -104.25) * mm, "mid": v(0.32, -122.08) * mm, "end": v(17.83, -103.6) * mm});
            skLineSegment(sketch, "E95.MirrorCS", {"start": v(17.83, -103.6) * mm, "end": v(17.83, -91.62) * mm});
            skLineSegment(sketch, "E96.MirrorCS", {"start": v(17.83, -91.62) * mm, "end": v(35.2, -74.25) * mm});
            skArc(sketch, "E97.0", {"start": v(-74.25, -64.25) * mm, "mid": v(-71.32, -71.32) * mm, "end": v(-64.25, -74.25) * mm});
            skLineSegment(sketch, "E97.1", {"start": v(-64.25, -74.25) * mm, "end": v(-35.86, -74.25) * mm});
            skArc(sketch, "E97.3", {"start": v(64.25, -74.25) * mm, "mid": v(71.32, -71.32) * mm, "end": v(74.25, -64.25) * mm});
            skArc(sketch, "E97.4", {"start": v(-64.25, 74.25) * mm, "mid": v(-71.32, 71.32) * mm, "end": v(-74.25, 64.25) * mm});
            skLineSegment(sketch, "E97.5", {"start": v(-64.25, 74.25) * mm, "end": v(-35.86, 74.25) * mm});
            skArc(sketch, "E97.6", {"start": v(74.25, 64.25) * mm, "mid": v(71.32, 71.32) * mm, "end": v(64.25, 74.25) * mm});
            skLineSegment(sketch, "E97.7", {"start": v(74.25, -64.25) * mm, "end": v(74.25, 64.25) * mm});
            skArc(sketch, "E98.0", {"start": v(-52.98, 45.17) * mm, "mid": v(-55.9, 42.58) * mm, "end": v(-57, 38.83) * mm});
            skArc(sketch, "E98.1", {"start": v(52.98, 45.17) * mm, "mid": v(0, 57) * mm, "end": v(-52.98, 45.17) * mm});
            skLineSegment(sketch, "E98.2", {"start": v(-57, 38.83) * mm, "end": v(-57, -38.83) * mm});
            skArc(sketch, "E98.3", {"start": v(57, 38.83) * mm, "mid": v(55.9, 42.58) * mm, "end": v(52.98, 45.17) * mm});
            skArc(sketch, "E98.4", {"start": v(-57, -38.83) * mm, "mid": v(-55.9, -42.58) * mm, "end": v(-52.98, -45.17) * mm});
            skArc(sketch, "E98.5", {"start": v(-52.98, -45.17) * mm, "mid": v(0, -57) * mm, "end": v(52.98, -45.17) * mm});
            skArc(sketch, "E98.6", {"start": v(52.98, -45.17) * mm, "mid": v(55.9, -42.58) * mm, "end": v(57, -38.83) * mm});
            skLineSegment(sketch, "E98.7", {"start": v(57, 38.83) * mm, "end": v(57, -38.83) * mm});
            skLineSegment(sketch, "E99.trimOffspring", {"start": v(35.2, -74.25) * mm, "end": v(64.25, -74.25) * mm});
            skLineSegment(sketch, "E100.trimOffspring", {"start": v(35.2, 74.25) * mm, "end": v(64.25, 74.25) * mm});
            skLineSegment(sketch, "E101", {"start": v(-74.25, 64.25) * mm, "end": v(-74.25, -64.25) * mm});
            skCircle(sketch, "E102.0", {"center": v(-60, -60) * mm, "radius": 4 * mm});
            skCircle(sketch, "E103.0", {"center": v(60, -60) * mm, "radius": 4 * mm});
            skCircle(sketch, "E104.0", {"center": v(-60, 60) * mm, "radius": 4 * mm});
            skCircle(sketch, "E105.0", {"center": v(60, 60) * mm, "radius": 4 * mm});
            skSolve(sketch);
        }
        {
            var Q0;
            Q0 = qSketchRegion(id + "F16", true);
            var Q1;
            Q1 = qBodyType(qCreatedBy(id + "F16" ,EDGE), BodyType.WIRE);
            extrude(context, id + "F17", {"entities" : qUnion([Q0]), "surfaceEntities" : qUnion([Q1]), "depth" : 9.53 * mm, "offsetDistance" : 25.4 * mm});
        }
    });
